# Revit family: Hager-Orion_Plus-IP66-D300-Cl.II-Poly_encl-630A-NoHosted-PL-pl
name_source: partatom
category: Electrical Equipment
units: mm (PartAtom-declared; Revit-internal decimal feet)

## family parameters
Always vertical = Yes
Cut with Voids When Loaded = No
Panel Configuration = Two Columns, Circuits Across
Part Type = Panelboard
Room Calculation Point = No
Round Connector Dimension = Use Diameter
Shared = No
Work Plane-Based = Yes

## types (2) — shared parameters
Default Elevation = 1219 mm
EF000003 - Sposób montażu = EV000384 - Montaż natynkowy
EF000007 - Kolor = EV000270 - Szary
EF000008 - Szerokość = 600 mm  [stored 1.9685 ft]
EF000040 - Wysokość = 800 mm  [stored 2.62467 ft]
EF000049 - Głębokość = 300 mm  [stored 0.984252 ft]
EF000116 - Numer RAL = 7035
EF000118 - Z płytą montażową = No
EF000339 - Rodzaj pokrywy = EV004216 - Drzwi
EF001088 - Możliwość rozbudowy = No
EF001131 - Głębokość wewnętrzna = 300 mm  [stored 0.984252 ft]
EF001596 - Materiał obudowy = EV000139 - Tworzywo sztuczne
EF002950 - Szerokość wyrażona liczbą modułów = 28
EF003532 - Do zastosowań zewnętrznych = Yes
EF004427 - Liczba modułów = 140
EF004464 - Rodzaj drzwi = EV002646 - Pojedynczy
EF005474 - Stopień ochrony (IP) = EV006422 - IP66
EF006306 - Z zamkiem = Yes
EF007800 - Do ochrony odgromowej = No
EF008873 - Prąd znamionowy (In) = 630 A
EF009212 - Wykonanie pokrywy = EV000116 - Zamknięty
EF015940 - Pokrywa z wyzwalaczem nadciśnieniowym = No
HG000002 - Z drzwiami lub pokrywą = Yes
HG000003 - Zakres = Orion Plus
HG000006 - Montaż podtynkowy = No
HG000009 - Drzwi dwuskrzydłowe = No
HG000010 - Drzwi asymetryczne = No
HG000023 - Obudowa dwusekcyjna = No
HG000024 - Wysokość części dolnej = 600 mm  [stored 1.9685 ft]
HG000026 - Stojąca = No
Manufacturer = Hager
Type Comments = Orion Plus
zero-valued in all types: EF000218 - Głębokość wbudowania, EF000437 - Liczba wejść kablowych, EF009554 - Liczba otworów pod flansze, HG000027 - Wysokość cokołu

## per-type parameters (varying)
| type | EF000266 - Liczba rzędów | EF004293 - Odporność udarowa | EF006244 - Transparentna pokrywa/drzwi | EF009170 - Obudowa z materiału o wysokiej wytrzymałości mechanicznej | EF009171 - Drzwi/pokrywa z materiału o wysokiej wytrzymałości mechanicznej | HG000004 - Referencja producenta |
| Montaż natynkowy IP66 S600 W800 G300  - FL229B | 4 | EV008784 - IK10 | No | 2 mm  [stored 0.00656168 ft] | 2 mm  [stored 0.00656168 ft] | FL229B |
| Montaż natynkowy IP66 S600 W800 G300  - FL279B | 5 | EV006814 - IK08 | Yes | 3 mm  [stored 0.00984252 ft] | 3 mm  [stored 0.00984252 ft] | FL279B |

note: [stored X ft] marks values corroborated as IEEE doubles in the binary element streams (Revit-internal decimal feet)

## geometry (parser evidence)
native form markers: Blend x4, Sweep x5
no freeform markers — native parametric forms only
